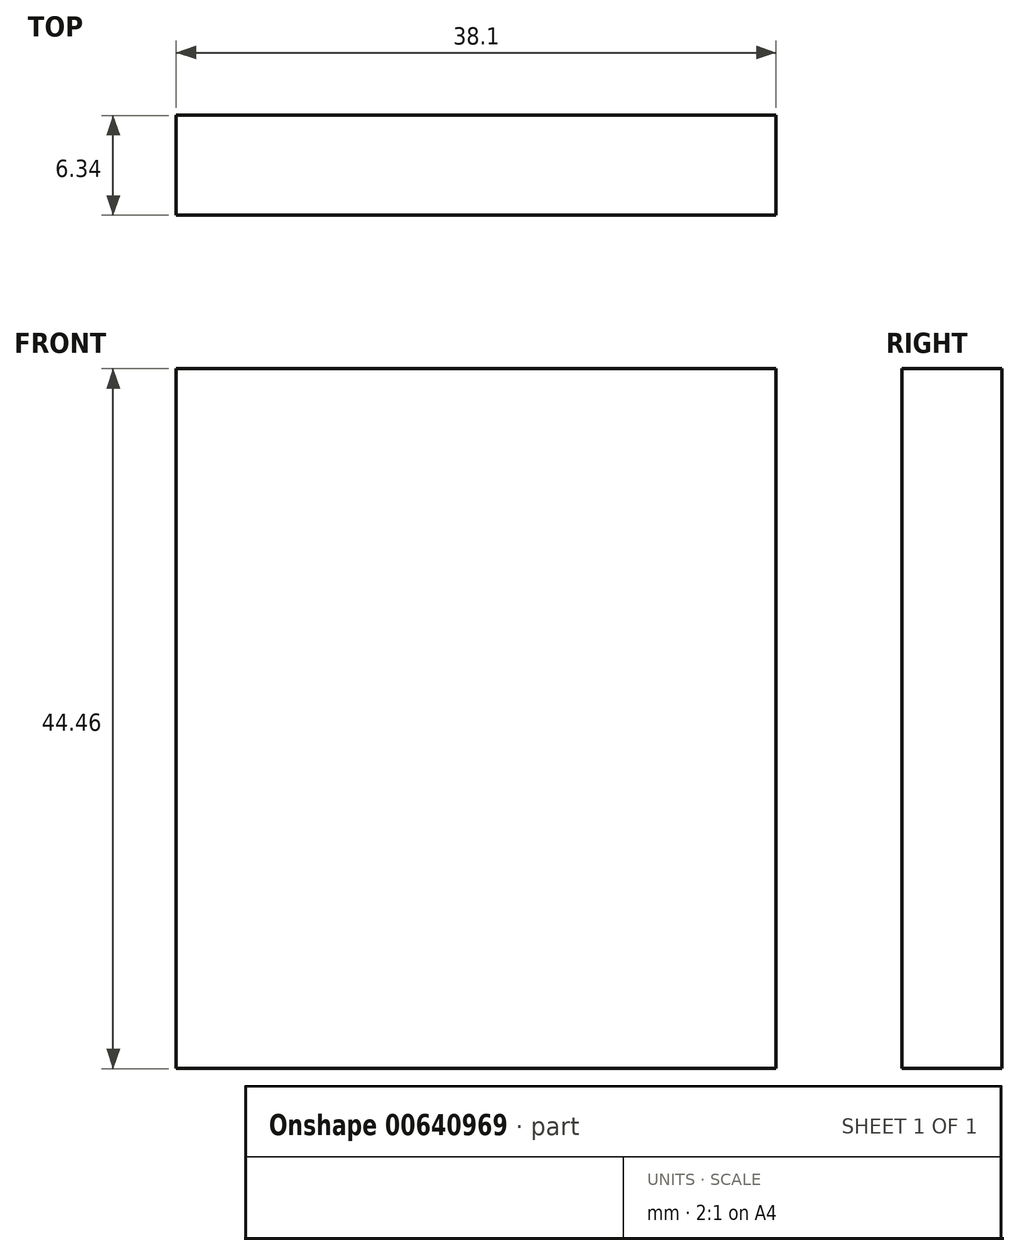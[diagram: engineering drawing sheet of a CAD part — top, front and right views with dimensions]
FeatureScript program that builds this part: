
annotation { "Feature Type Name" : "Feature", "Feature Type Description" : "" }
export const myFeature = defineFeature(function(context is Context, id is Id, definition is map)
    precondition{}
    {
        {
            var Q0;
            Q0=qCreatedBy(makeId("Front.planeOp"),FACE);
            var sketch = newSketch(context, id + "F0", { "sketchPlane" : qUnion([Q0])});
            skLineSegment(sketch, "E0.bottom", {"start": v(-19.05, 22.23) * mm, "end": v(19.05, 22.23) * mm});
            skLineSegment(sketch, "E0.top", {"start": v(-19.05, -22.23) * mm, "end": v(19.05, -22.23) * mm});
            skLineSegment(sketch, "E0.left", {"start": v(-19.05, 22.23) * mm, "end": v(-19.05, -22.23) * mm});
            skLineSegment(sketch, "E0.right", {"start": v(19.05, 22.23) * mm, "end": v(19.05, -22.23) * mm});
            skSolve(sketch);
        }
        {
            var Q0;
            Q0=makeQuery(id+"F0.imprint","IMPRINT",FACE,{"disambiguationData":[TD([[makeQuery(id+"F0.imprint","IMPRINT",EDGE,{"derivedFrom":sQuery(id+"F0.wireOp",EDGE,"E0.bottom")}),-1.0]])]});
            extrude(context, id + "F1", {"entities" : qUnion([Q0]), "endBound" : BoundingType.SYMMETRIC, "depth" : 6.35 * mm, "offsetDistance" : 25.4 * mm});
        }
    });
